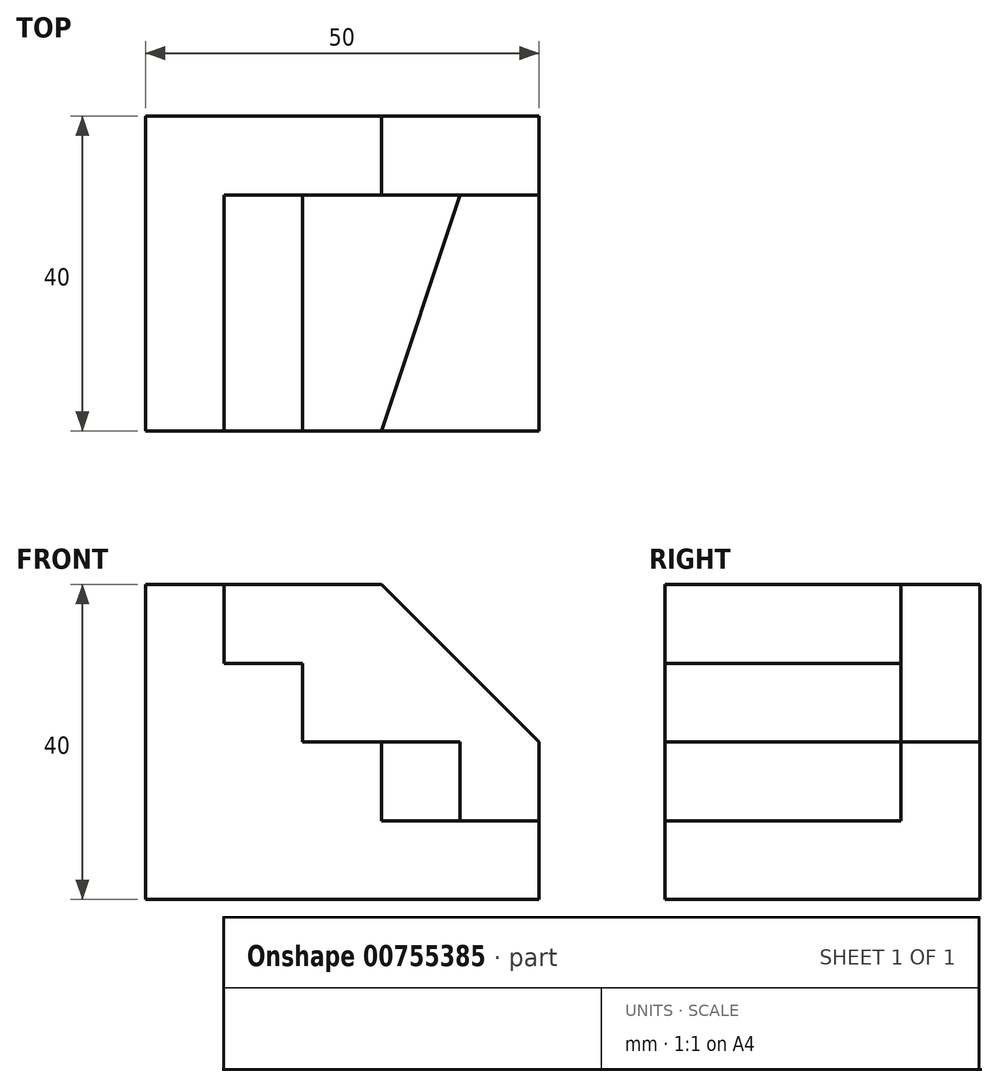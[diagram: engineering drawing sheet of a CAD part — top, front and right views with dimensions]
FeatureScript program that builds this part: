
annotation { "Feature Type Name" : "Feature", "Feature Type Description" : "" }
export const myFeature = defineFeature(function(context is Context, id is Id, definition is map)
    precondition{}
    {
        {
            var Q0;
            Q0=qCreatedBy(makeId("Front.planeOp"),FACE);
            var sketch = newSketch(context, id + "F0", { "sketchPlane" : qUnion([Q0])});
            skLineSegment(sketch, "E0", {"start": v(0, 0) * mm, "end": v(50, 0) * mm});
            skLineSegment(sketch, "E1", {"start": v(50, 0) * mm, "end": v(50, 40) * mm});
            skLineSegment(sketch, "E2", {"start": v(50, 40) * mm, "end": v(0, 40) * mm});
            skLineSegment(sketch, "E3", {"start": v(0, 40) * mm, "end": v(0, 0) * mm});
            skSolve(sketch);
        }
        {
            var Q0;
            Q0=makeQuery(id+"F0.imprint","IMPRINT",FACE,{"disambiguationData":[TD([[makeQuery(id+"F0.imprint","IMPRINT",EDGE,{"derivedFrom":sQuery(id+"F0.wireOp",EDGE,"E0")}),1.0]])]});
            extrude(context, id + "F1", {"entities" : qUnion([Q0]), "depth" : 40 * mm, "offsetDistance" : 25 * mm});
        }
        {
            var Q0;
            Q0=makeQuery(id+"F1.opExtrude","CAP_FACE",FACE,{"disambiguationData":[OSD([sQuery(id+"F0.wireOp",EDGE,"E0"),sQuery(id+"F0.wireOp",EDGE,"E1"),sQuery(id+"F0.wireOp",EDGE,"E2"),sQuery(id+"F0.wireOp",EDGE,"E3")])],"isStart":false});
            var sketch = newSketch(context, id + "F2", { "sketchPlane" : qUnion([Q0])});
            skLineSegment(sketch, "E4", {"start": v(50, 40) * mm, "end": v(10, 40) * mm});
            skLineSegment(sketch, "E5", {"start": v(10, 40) * mm, "end": v(10, 30) * mm});
            skLineSegment(sketch, "E6", {"start": v(10, 30) * mm, "end": v(20, 30) * mm});
            skLineSegment(sketch, "E7", {"start": v(20, 30) * mm, "end": v(20, 20) * mm});
            skLineSegment(sketch, "E8", {"start": v(20, 20) * mm, "end": v(40, 20) * mm});
            skLineSegment(sketch, "E9", {"start": v(40, 20) * mm, "end": v(40, 10) * mm});
            skLineSegment(sketch, "E10", {"start": v(40, 10) * mm, "end": v(50, 10) * mm});
            skLineSegment(sketch, "E11", {"start": v(50, 10) * mm, "end": v(50, 40) * mm});
            skSolve(sketch);
        }
        {
            var Q0;
            Q0=makeQuery(id+"F2.imprint","IMPRINT",FACE,{"disambiguationData":[TD([[makeQuery(id+"F2.imprint","IMPRINT",EDGE,{"derivedFrom":sQuery(id+"F2.wireOp",EDGE,"E4")}),1.0]])]});
            extrude(context, id + "F3", {"entities" : qUnion([Q0]), "operationType" : NewBodyOperationType.REMOVE, "oppositeDirection" : true, "depth" : 30 * mm, "offsetDistance" : 25 * mm});
        }
        {
            var Q0;
            Q0=makeQuery(id+"F3.boolean.opBoolean","COPY",FACE,{"derivedFrom":makeQuery(id+"F3.opExtrude","CAP_FACE",FACE,{"disambiguationData":[OSD([sQuery(id+"F2.wireOp",EDGE,"E4"),sQuery(id+"F2.wireOp",EDGE,"E5"),sQuery(id+"F2.wireOp",EDGE,"E6"),sQuery(id+"F2.wireOp",EDGE,"E7"),sQuery(id+"F2.wireOp",EDGE,"E8"),sQuery(id+"F2.wireOp",EDGE,"E9"),sQuery(id+"F2.wireOp",EDGE,"E10"),sQuery(id+"F2.wireOp",EDGE,"E11")])],"isStart":false})});
            var sketch = newSketch(context, id + "F4", { "sketchPlane" : qUnion([Q0])});
            skLineSegment(sketch, "E12", {"start": v(50, 40) * mm, "end": v(30, 40) * mm});
            skLineSegment(sketch, "E13", {"start": v(30, 40) * mm, "end": v(50, 20) * mm});
            skLineSegment(sketch, "E14", {"start": v(50, 20) * mm, "end": v(50, 40) * mm});
            skSolve(sketch);
        }
        {
            var Q0;
            Q0=makeQuery(id+"F4.imprint","IMPRINT",FACE,{"disambiguationData":[TD([[makeQuery(id+"F4.imprint","IMPRINT",EDGE,{"derivedFrom":sQuery(id+"F4.wireOp",EDGE,"E12")}),1.0]])]});
            extrude(context, id + "F5", {"entities" : qUnion([Q0]), "operationType" : NewBodyOperationType.REMOVE, "oppositeDirection" : true, "depth" : 10 * mm, "offsetDistance" : 25 * mm});
        }
        {
            var Q0;
            Q0=makeQuery(id+"F3.boolean.opBoolean","COPY",FACE,{"derivedFrom":makeQuery(id+"F3.opExtrude","SWEPT_FACE",FACE,{"disambiguationData":[OSD([sQuery(id+"F2.wireOp",EDGE,"E8")])]})});
            var sketch = newSketch(context, id + "F6", { "sketchPlane" : qUnion([Q0])});
            skLineSegment(sketch, "E15", {"start": v(40, -10) * mm, "end": v(30, -40) * mm});
            skLineSegment(sketch, "E16", {"start": v(30, -40) * mm, "end": v(40, -40) * mm});
            skLineSegment(sketch, "E17", {"start": v(40, -40) * mm, "end": v(40, -10) * mm});
            skSolve(sketch);
        }
        {
            var Q0;
            Q0=makeQuery(id+"F6.imprint","IMPRINT",FACE,{"disambiguationData":[TD([[makeQuery(id+"F6.imprint","IMPRINT",EDGE,{"derivedFrom":sQuery(id+"F6.wireOp",EDGE,"E15")}),1.0]])]});
            extrude(context, id + "F7", {"entities" : qUnion([Q0]), "operationType" : NewBodyOperationType.REMOVE, "oppositeDirection" : true, "depth" : 10 * mm, "offsetDistance" : 25 * mm});
        }
    });
